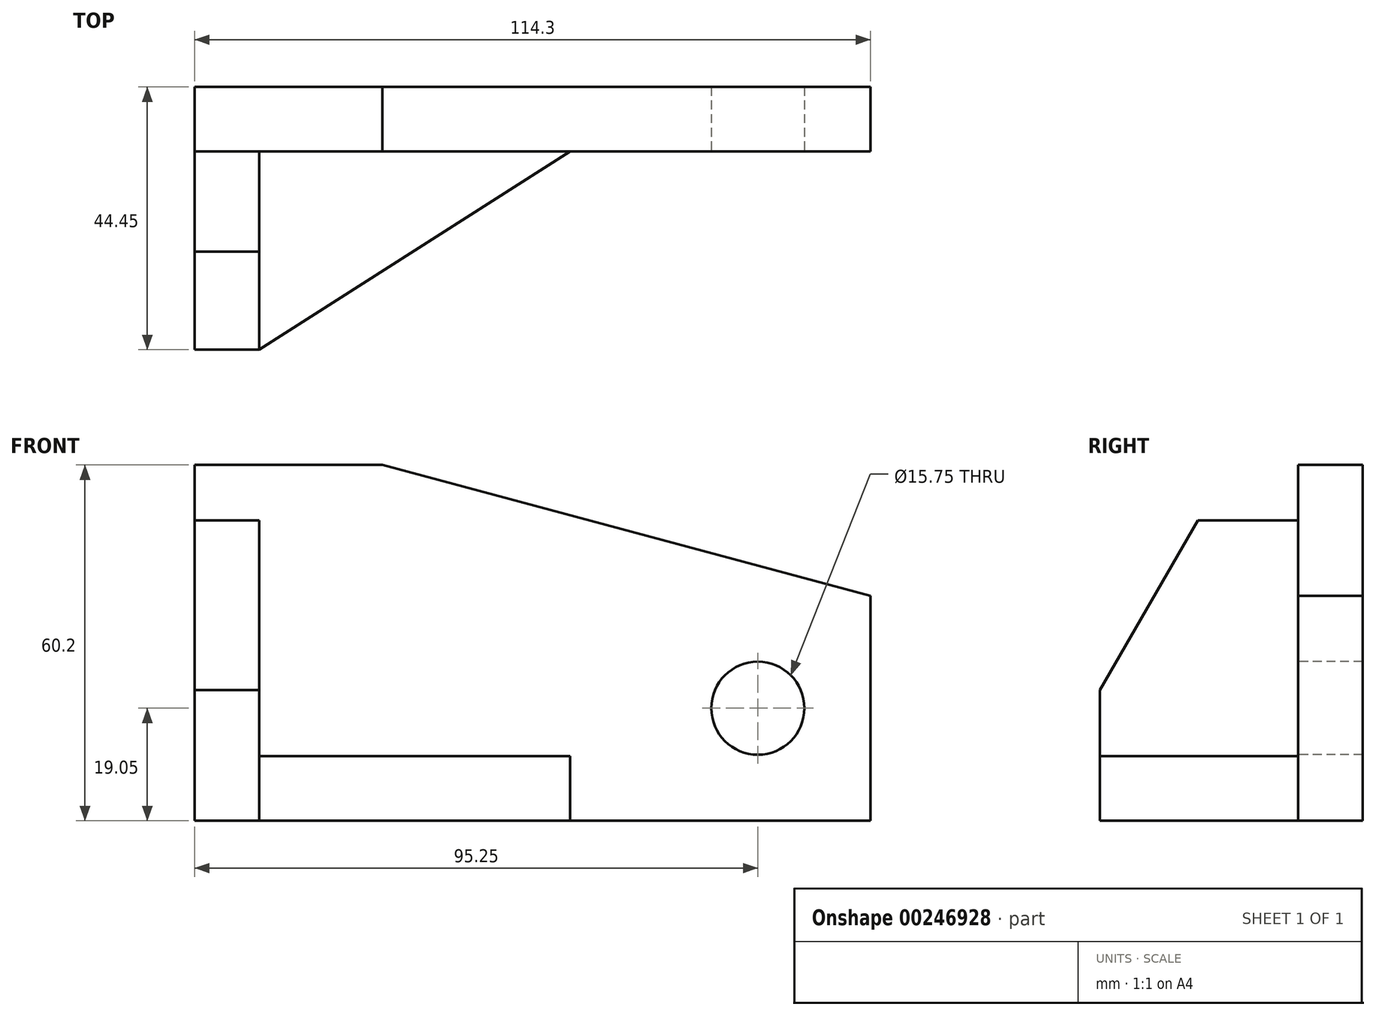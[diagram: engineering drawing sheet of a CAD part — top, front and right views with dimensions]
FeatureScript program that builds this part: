
annotation { "Feature Type Name" : "Feature", "Feature Type Description" : "" }
export const myFeature = defineFeature(function(context is Context, id is Id, definition is map)
    precondition{}
    {
        {
            var Q0;
            Q0=qCreatedBy(makeId("Front.planeOp"),FACE);
            var sketch = newSketch(context, id + "F0", { "sketchPlane" : qUnion([Q0])});
            skLineSegment(sketch, "E0", {"start": v(0, 0) * mm, "end": v(-57.15, 0) * mm});
            skLineSegment(sketch, "E1", {"start": v(0, 0) * mm, "end": v(57.15, 0) * mm});
            skLineSegment(sketch, "E2", {"start": v(-57.15, 0) * mm, "end": v(-57.15, 60.2) * mm});
            skLineSegment(sketch, "E3", {"start": v(-57.15, 60.2) * mm, "end": v(-25.4, 60.2) * mm});
            skLineSegment(sketch, "E4", {"start": v(57.15, 0) * mm, "end": v(57.15, 38.08) * mm});
            skLineSegment(sketch, "E5", {"start": v(-25.4, 60.2) * mm, "end": v(57.15, 38.08) * mm});
            skSolve(sketch);
        }
        {
            var Q0;
            Q0=makeQuery(id+"F0.imprint","IMPRINT",FACE,{"disambiguationData":[TD([[makeQuery(id+"F0.imprint","IMPRINT",EDGE,{"derivedFrom":sQuery(id+"F0.wireOp",EDGE,"E0")}),-1.0]])]});
            extrude(context, id + "F1", {"entities" : qUnion([Q0]), "depth" : 10.92 * mm});
        }
        {
            var Q0;
            Q0=makeQuery(id+"F1.opExtrude","SWEPT_FACE",FACE,{"disambiguationData":[OSD([sQuery(id+"F0.wireOp",EDGE,"E2")])]});
            var sketch = newSketch(context, id + "F2", { "sketchPlane" : qUnion([Q0])});
            skLineSegment(sketch, "E6", {"start": v(10.92, 0) * mm, "end": v(44.45, 0) * mm});
            skLineSegment(sketch, "E7", {"start": v(10.92, 0) * mm, "end": v(10.92, 50.8) * mm});
            skLineSegment(sketch, "E8", {"start": v(44.45, 22.1) * mm, "end": v(44.45, 0) * mm});
            skLineSegment(sketch, "E9", {"start": v(10.92, 50.8) * mm, "end": v(27.88, 50.8) * mm});
            skLineSegment(sketch, "E10", {"start": v(27.88, 50.8) * mm, "end": v(44.45, 22.1) * mm});
            skSolve(sketch);
        }
        {
            var Q0;
            Q0=makeQuery(id+"F2.imprint","IMPRINT",FACE,{"disambiguationData":[TD([[makeQuery(id+"F2.imprint","IMPRINT",EDGE,{"derivedFrom":sQuery(id+"F2.wireOp",EDGE,"E6")}),1.0]])]});
            extrude(context, id + "F3", {"entities" : qUnion([Q0]), "operationType" : NewBodyOperationType.ADD, "oppositeDirection" : true, "depth" : 10.92 * mm});
        }
        {
            var Q0;
            Q0=makeQuery(id+"F3.boolean.opBoolean","MERGE",FACE,{"derivedFrom":[makeQuery(id+"F1.opExtrude","SWEPT_FACE",FACE,{"disambiguationData":[OSD([sQuery(id+"F0.wireOp",EDGE,"E0"),sQuery(id+"F0.wireOp",EDGE,"E1")])]}),makeQuery(id+"F3.opExtrude","SWEPT_FACE",FACE,{"disambiguationData":[OSD([sQuery(id+"F2.wireOp",EDGE,"E6")])]})]});
            var sketch = newSketch(context, id + "F4", { "sketchPlane" : qUnion([Q0])});
            skLineSegment(sketch, "E11", {"start": v(-46.23, 10.92) * mm, "end": v(6.35, 10.92) * mm});
            skLineSegment(sketch, "E12", {"start": v(-46.23, 10.92) * mm, "end": v(-46.23, 44.45) * mm});
            skLineSegment(sketch, "E13", {"start": v(-46.23, 44.45) * mm, "end": v(6.35, 10.92) * mm});
            skSolve(sketch);
        }
        {
            var Q0;
            Q0=makeQuery(id+"F4.imprint","IMPRINT",FACE,{"disambiguationData":[TD([[makeQuery(id+"F4.imprint","IMPRINT",EDGE,{"derivedFrom":sQuery(id+"F4.wireOp",EDGE,"E11")}),-1.0]])]});
            extrude(context, id + "F5", {"entities" : qUnion([Q0]), "operationType" : NewBodyOperationType.ADD, "oppositeDirection" : true, "depth" : 10.92 * mm});
        }
        {
            var Q0;
            Q0=makeQuery(id+"F1.opExtrude","CAP_FACE",FACE,{"disambiguationData":[OSD([sQuery(id+"F0.wireOp",EDGE,"E0"),sQuery(id+"F0.wireOp",EDGE,"E1"),sQuery(id+"F0.wireOp",EDGE,"E2"),sQuery(id+"F0.wireOp",EDGE,"E3"),sQuery(id+"F0.wireOp",EDGE,"E4"),sQuery(id+"F0.wireOp",EDGE,"E5")])],"isStart":false});
            var sketch = newSketch(context, id + "F6", { "sketchPlane" : qUnion([Q0])});
            skLineSegment(sketch, "E14", {"start": v(57.15, 0) * mm, "end": v(38.1, 0) * mm, "construction": true});
            skLineSegment(sketch, "E15", {"start": v(38.1, 0) * mm, "end": v(38.1, 19.05) * mm, "construction": true});
            skCircle(sketch, "E16", {"center": v(38.1, 19.05) * mm, "radius": 7.87 * mm});
            skSolve(sketch);
        }
        {
            var Q0;
            Q0=makeQuery(id+"F6.imprint","IMPRINT",FACE,{"disambiguationData":[TD([[makeQuery(id+"F6.imprint","IMPRINT",EDGE,{"derivedFrom":sQuery(id+"F6.wireOp",EDGE,"E16")}),1.0]])]});
            extrude(context, id + "F7", {"entities" : qUnion([Q0]), "operationType" : NewBodyOperationType.REMOVE, "oppositeDirection" : true, "depth" : 10.92 * mm});
        }
    });
